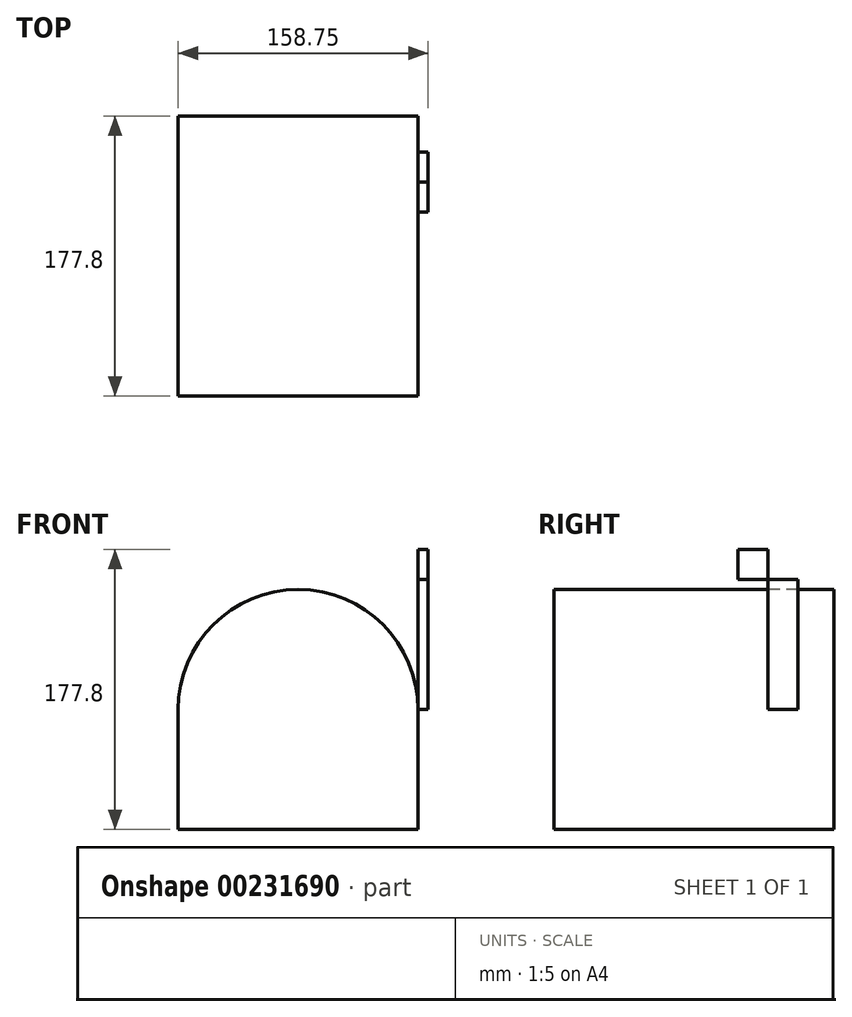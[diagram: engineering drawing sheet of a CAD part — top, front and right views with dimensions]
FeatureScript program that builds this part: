
annotation { "Feature Type Name" : "Feature", "Feature Type Description" : "" }
export const myFeature = defineFeature(function(context is Context, id is Id, definition is map)
    precondition{}
    {
        {
            var Q0;
            Q0=qCreatedBy(makeId("Right.planeOp"),FACE);
            var sketch = newSketch(context, id + "F0", { "sketchPlane" : qUnion([Q0])});
            skLineSegment(sketch, "E0.bottom", {"start": v(-77.7, 0) * mm, "end": v(100.1, 0) * mm});
            skLineSegment(sketch, "E0.top", {"start": v(-77.7, 76.2) * mm, "end": v(100.1, 76.2) * mm});
            skLineSegment(sketch, "E0.left", {"start": v(-77.7, 0) * mm, "end": v(-77.7, 76.2) * mm});
            skLineSegment(sketch, "E0.right", {"start": v(100.1, 0) * mm, "end": v(100.1, 76.2) * mm});
            skSolve(sketch);
        }
        {
            var Q0;
            Q0 = qSketchRegion(id + "F0", true);
            var Q1;
            Q1=sQuery(id+"F0.wireOp",EDGE,"E0.bottom");
            revolve(context, id + "F1", {"entities" : qUnion([Q0]), "axis" : qUnion([Q1]), "revolveType" : RevolveType.FULL});
        }
        {
            var Q0;
            Q0=makeQuery(id+"F1.opRevolve","SWEPT_FACE",FACE,{"disambiguationData":[OSD([sQuery(id+"F0.wireOp",EDGE,"E0.left")])]});
            var sketch = newSketch(context, id + "F2", { "sketchPlane" : qUnion([Q0])});
            skLineSegment(sketch, "E1.bottom", {"start": v(0, 0) * mm, "end": v(76.2, 0) * mm});
            skLineSegment(sketch, "E1.top", {"start": v(0, -76.2) * mm, "end": v(76.2, -76.2) * mm});
            skLineSegment(sketch, "E1.left", {"start": v(0, 0) * mm, "end": v(0, -76.2) * mm});
            skLineSegment(sketch, "E1.right", {"start": v(76.2, 0) * mm, "end": v(76.2, -76.2) * mm});
            skLineSegment(sketch, "E2.bottom", {"start": v(0, 0) * mm, "end": v(-76.2, 0) * mm});
            skLineSegment(sketch, "E2.top", {"start": v(0, -76.2) * mm, "end": v(-76.2, -76.2) * mm});
            skLineSegment(sketch, "E2.right", {"start": v(-76.2, 0) * mm, "end": v(-76.2, -76.2) * mm});
            skSolve(sketch);
        }
        {
            var Q0;
            {var subQ0=sQuery(id+"F2.wireOp",EDGE,"E2.bottom");Q0=makeQuery(id+"F2.imprint","IMPRINT",FACE,{"disambiguationData":[TD([[makeQuery(id+"F2.imprint","IMPRINT",EDGE,{"derivedFrom":subQ0}),1.0]])]});}
            var Q1;
            {var subQ0=sQuery(id+"F2.wireOp",EDGE,"E1.bottom");Q1=makeQuery(id+"F2.imprint","IMPRINT",FACE,{"disambiguationData":[TD([[makeQuery(id+"F2.imprint","IMPRINT",EDGE,{"derivedFrom":subQ0}),-1.0]])]});}
            var Q2;
            {var subQ0=sQuery(id+"F2.wireOp",EDGE,"E1.top");Q2=makeQuery(id+"F2.imprint","IMPRINT",FACE,{"disambiguationData":[TD([[makeQuery(id+"F2.imprint","IMPRINT",EDGE,{"derivedFrom":subQ0}),1.0]])]});}
            var Q3;
            {var subQ0=sQuery(id+"F2.wireOp",EDGE,"E2.top");Q3=makeQuery(id+"F2.imprint","IMPRINT",FACE,{"disambiguationData":[TD([[makeQuery(id+"F2.imprint","IMPRINT",EDGE,{"derivedFrom":subQ0}),-1.0]])]});}
            extrude(context, id + "F3", {"entities" : qUnion([Q0, Q1, Q2, Q3]), "operationType" : NewBodyOperationType.ADD, "oppositeDirection" : true, "depth" : 177.8 * mm});
        }
        {
            var Q0;
            Q0=makeQuery(id+"F3.opExtrude","SWEPT_FACE",FACE,{"disambiguationData":[OSD([sQuery(id+"F2.wireOp",EDGE,"E1.right")])]});
            var sketch = newSketch(context, id + "F4", { "sketchPlane" : qUnion([Q0])});
            skLineSegment(sketch, "E3.bottom", {"start": v(58.24, 0) * mm, "end": v(77.29, 0) * mm});
            skLineSegment(sketch, "E3.top", {"start": v(58.24, 101.6) * mm, "end": v(77.29, 101.6) * mm});
            skLineSegment(sketch, "E3.left", {"start": v(58.24, 0) * mm, "end": v(58.24, 101.6) * mm});
            skLineSegment(sketch, "E3.right", {"start": v(77.29, 0) * mm, "end": v(77.29, 101.6) * mm});
            skLineSegment(sketch, "E4.bottom", {"start": v(77.29, 101.6) * mm, "end": v(39.19, 101.6) * mm});
            skLineSegment(sketch, "E4.top", {"start": v(77.29, 82.55) * mm, "end": v(39.19, 82.55) * mm});
            skLineSegment(sketch, "E4.left", {"start": v(77.29, 101.6) * mm, "end": v(77.29, 82.55) * mm});
            skLineSegment(sketch, "E4.right", {"start": v(39.19, 101.6) * mm, "end": v(39.19, 82.55) * mm});
            skSolve(sketch);
        }
        {
            var Q0;
            {var subQ5=sQuery(id+"F4.wireOp",EDGE,"E4.right");Q0=makeQuery(id+"F4.imprint","IMPRINT",FACE,{"disambiguationData":[TD([[makeQuery(id+"F4.imprint","IMPRINT",EDGE,{"derivedFrom":subQ5}),1.0]])]});}
            var Q1;
            {var subQ5=sQuery(id+"F4.wireOp",EDGE,"E4.left");Q1=makeQuery(id+"F4.imprint","IMPRINT",FACE,{"disambiguationData":[TD([[makeQuery(id+"F4.imprint","IMPRINT",EDGE,{"derivedFrom":subQ5}),-1.0]])]});}
            var Q2;
            {var subQ0=sQuery(id+"F4.wireOp",EDGE,"E3.bottom");Q2=makeQuery(id+"F4.imprint","IMPRINT",FACE,{"disambiguationData":[TD([[makeQuery(id+"F4.imprint","IMPRINT",EDGE,{"derivedFrom":subQ0}),-1.0]])]});}
            extrude(context, id + "F5", {"entities" : qUnion([Q0, Q1, Q2]), "depth" : 6.35 * mm});
        }
    });
